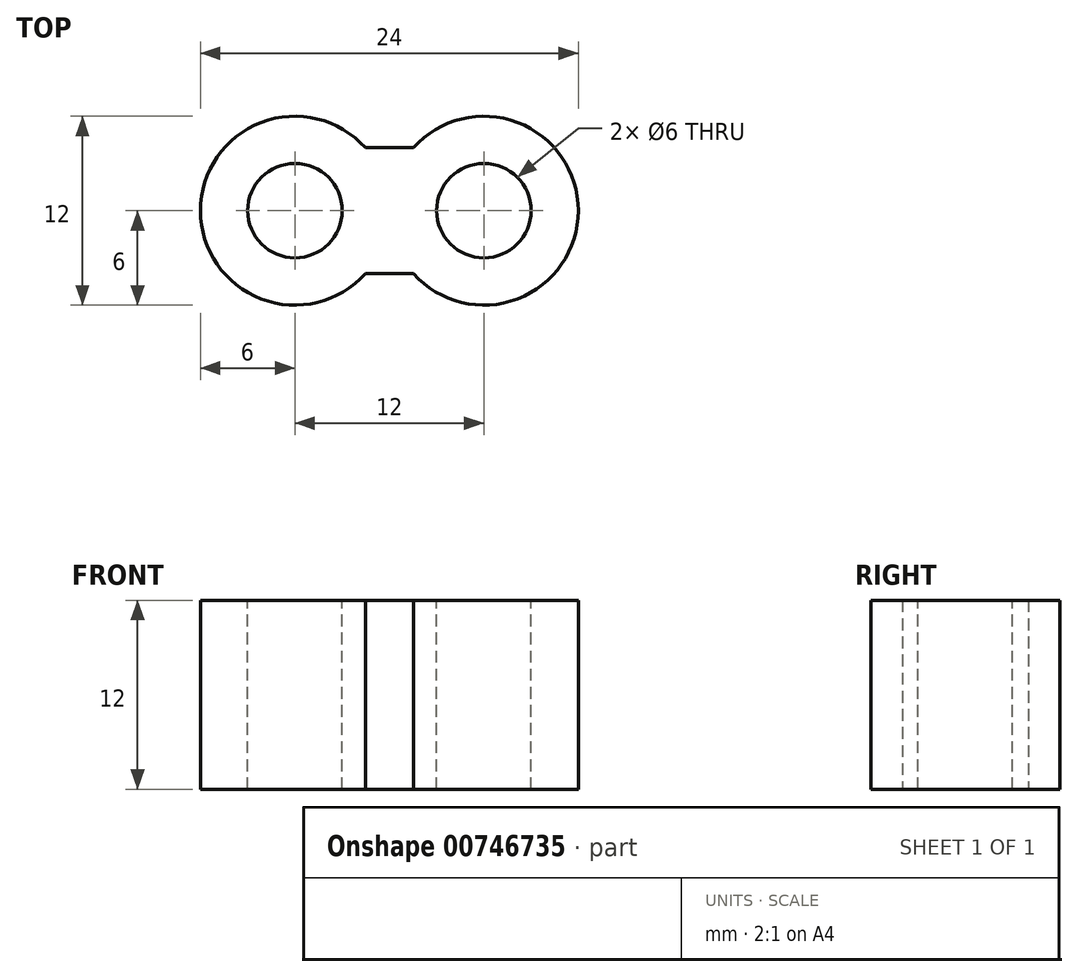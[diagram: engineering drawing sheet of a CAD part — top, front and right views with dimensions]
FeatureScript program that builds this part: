
annotation { "Feature Type Name" : "Feature", "Feature Type Description" : "" }
export const myFeature = defineFeature(function(context is Context, id is Id, definition is map)
    precondition{}
    {
        {
            var Q0;
            Q0=qCreatedBy(makeId("Top.planeOp"),FACE);
            var sketch = newSketch(context, id + "F0", { "sketchPlane" : qUnion([Q0])});
            skPoint(sketch, "E0", {"position": v(-6, 0) * mm});
            skPoint(sketch, "E1", {"position": v(6, 0) * mm});
            skCircle(sketch, "E2", {"center": v(-6, 0) * mm, "radius": 6 * mm});
            skCircle(sketch, "E3", {"center": v(6, 0) * mm, "radius": 6 * mm});
            skPoint(sketch, "E4", {"position": v(0, 4) * mm});
            skPoint(sketch, "E5", {"position": v(0, -4) * mm});
            skLineSegment(sketch, "E6", {"start": v(1.53, 4) * mm, "end": v(-1.53, 4) * mm});
            skLineSegment(sketch, "E7", {"start": v(0, -4) * mm, "end": v(1.53, -4) * mm});
            skLineSegment(sketch, "E8", {"start": v(1.53, -4) * mm, "end": v(-1.53, -4) * mm});
            skSolve(sketch);
        }
        {
            var Q0;
            Q0 = qSketchRegion(id + "F0", true);
            extrude(context, id + "F1", {"entities" : qUnion([Q0]), "depth" : 12 * mm, "offsetDistance" : 25 * mm});
        }
        {
            var Q0;
            Q0=makeQuery(id+"F1.opExtrude","CAP_FACE",FACE,{"disambiguationData":[OSD([sQuery(id+"F0.wireOp",EDGE,"E2"),sQuery(id+"F0.wireOp",EDGE,"E3"),sQuery(id+"F0.wireOp",EDGE,"E6"),sQuery(id+"F0.wireOp",EDGE,"E8")])],"isStart":false});
            var sketch = newSketch(context, id + "F2", { "sketchPlane" : qUnion([Q0])});
            skPoint(sketch, "E9", {"position": v(-6, 0) * mm});
            skPoint(sketch, "E10", {"position": v(6, 0) * mm});
            skCircle(sketch, "E11", {"center": v(-6, 0) * mm, "radius": 3 * mm});
            skCircle(sketch, "E12", {"center": v(6, 0) * mm, "radius": 3 * mm});
            skSolve(sketch);
        }
        {
            var Q0;
            Q0 = qSketchRegion(id + "F2", true);
            extrude(context, id + "F3", {"entities" : qUnion([Q0]), "operationType" : NewBodyOperationType.REMOVE, "endBound" : BoundingType.THROUGH_ALL, "oppositeDirection" : true, "depth" : 25 * mm, "offsetDistance" : 25 * mm});
        }
    });
